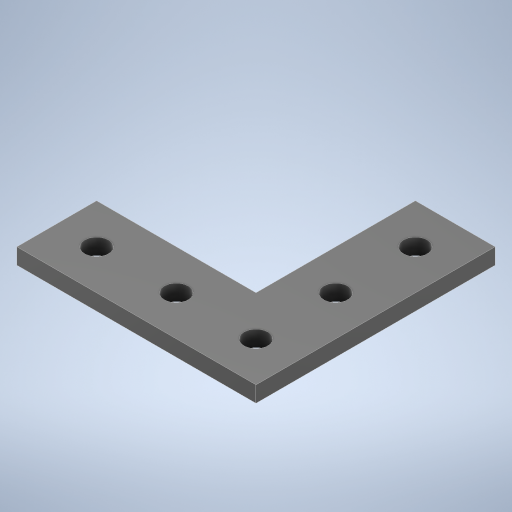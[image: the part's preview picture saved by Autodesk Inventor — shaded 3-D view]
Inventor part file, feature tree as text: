
AUTODESK INVENTOR PART (.ipt)
format: ipt  version: 2024 (Build 280153000, 153)  size: 256,512 bytes
history: native  units: in
note: dims shown in document units (in); Inventor stores cm internally (conversion verified against a paired STEP export)
features: extrude x1, sketch x1
ambient origin geometry x8: Origin, YZ Plane, XZ Plane, XY Plane, X Axis, Y Axis, Z Axis, Center Point
bodies: Solid1 (feature_tree)
feature tree (2):
  extrude  "Extrusion1"  Depth=3.0in
  sketch  "Sketch1"  dims[d0=1.0in d1=3.0in d2=3.0in d3=1.0in d4=1.0in d5=1.0in d6=1.0in d7=1.0in d8=0.3in d9=0.3in d10=0.3in d11=0.3in d12=0.3in d13=0.2in d14=0.0in]
